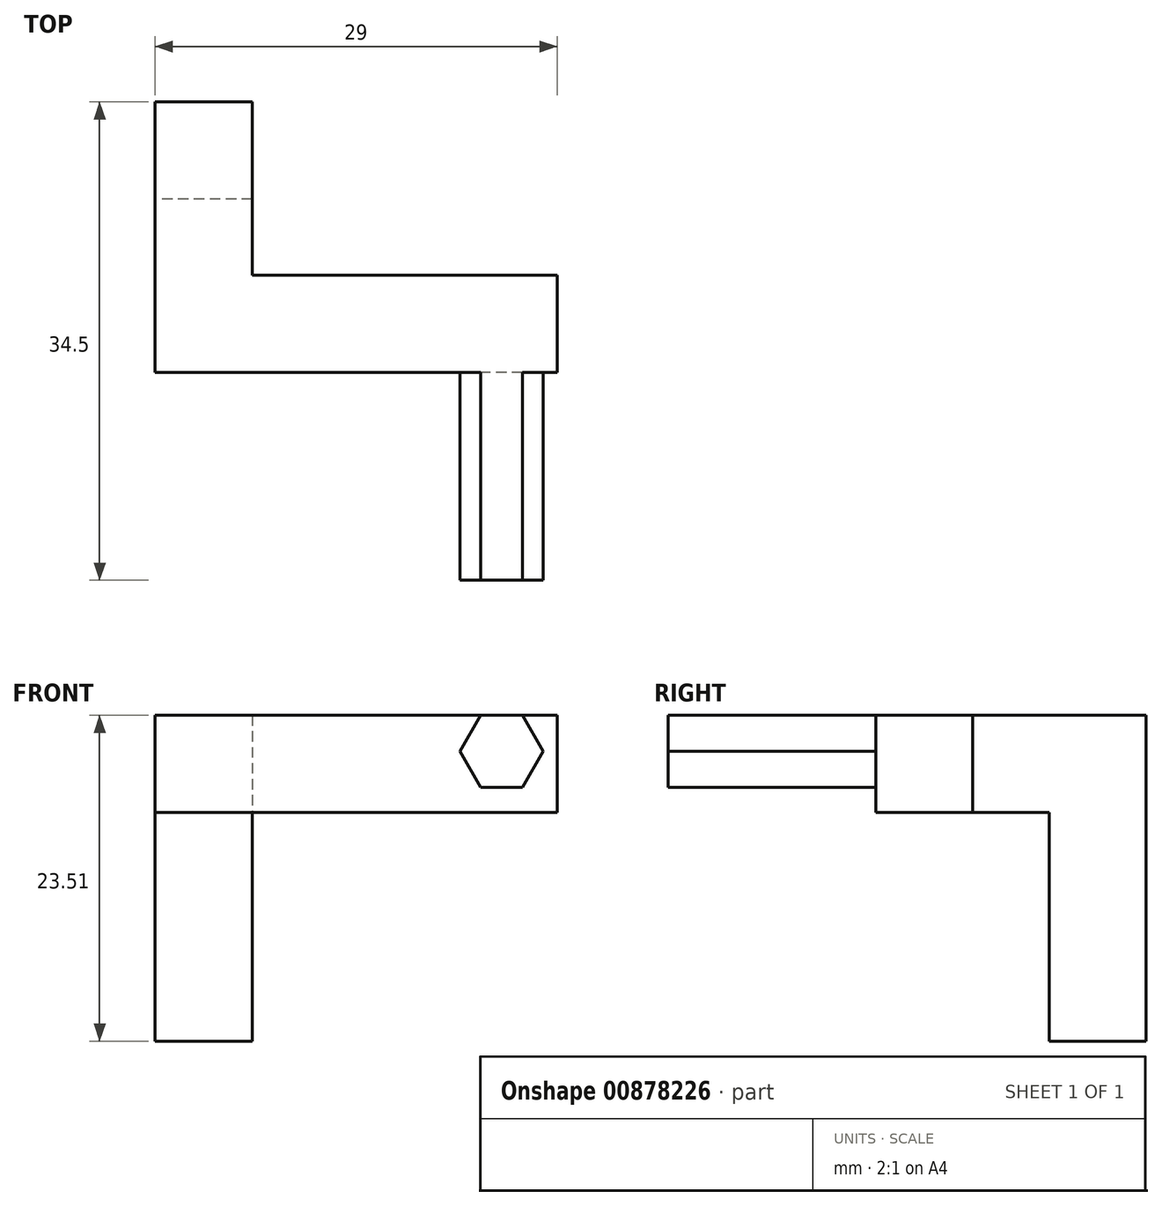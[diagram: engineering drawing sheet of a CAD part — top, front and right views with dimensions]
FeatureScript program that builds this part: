
annotation { "Feature Type Name" : "Feature", "Feature Type Description" : "" }
export const myFeature = defineFeature(function(context is Context, id is Id, definition is map)
    precondition{}
    {
        {
            var Q0;
            Q0=qCreatedBy(makeId("Top.planeOp"),FACE);
            var sketch = newSketch(context, id + "F0", { "sketchPlane" : qUnion([Q0])});
            skLineSegment(sketch, "E0.bottom", {"start": v(3.5, -3.5) * mm, "end": v(-3.5, -3.5) * mm});
            skLineSegment(sketch, "E0.top", {"start": v(3.5, 3.5) * mm, "end": v(-3.5, 3.5) * mm});
            skLineSegment(sketch, "E0.left", {"start": v(3.5, -3.5) * mm, "end": v(3.5, 3.5) * mm});
            skLineSegment(sketch, "E0.right", {"start": v(-3.5, -3.5) * mm, "end": v(-3.5, 3.5) * mm});
            skPoint(sketch, "E0.middle", {"position": v(0, 0) * mm});
            skSolve(sketch);
        }
        {
            var Q0;
            Q0 = qSketchRegion(id + "F0", true);
            extrude(context, id + "F1", {"entities" : qUnion([Q0]), "oppositeDirection" : true, "depth" : 16.5 * mm, "offsetDistance" : 25.4 * mm});
        }
        {
            var Q0;
            Q0=qCreatedBy(makeId("Top.planeOp"),FACE);
            var sketch = newSketch(context, id + "F2", { "sketchPlane" : qUnion([Q0])});
            skLineSegment(sketch, "E1", {"start": v(0, 0) * mm, "end": v(0, -16) * mm});
            skLineSegment(sketch, "E2", {"start": v(0, -16) * mm, "end": v(25.5, -16) * mm});
            skSolve(sketch);
        }
        {
            var Q0;
            Q0=makeQuery(id+"F1.opExtrude","SWEPT_FACE",FACE,{"disambiguationData":[OSD([sQuery(id+"F0.wireOp",EDGE,"E0.top")])]});
            var sketch = newSketch(context, id + "F3", { "sketchPlane" : qUnion([Q0])});
            skLineSegment(sketch, "E3.0.0", {"start": v(3.5, 0) * mm, "end": v(-3.5, 0) * mm, "construction": true});
            skLineSegment(sketch, "E3.0.1", {"start": v(-3.5, 0) * mm, "end": v(-3.5, -16.51) * mm, "construction": true});
            skLineSegment(sketch, "E3.0.2", {"start": v(-3.5, -16.51) * mm, "end": v(3.5, -16.51) * mm, "construction": true});
            skLineSegment(sketch, "E3.0.3", {"start": v(3.5, -16.51) * mm, "end": v(3.5, 0) * mm, "construction": true});
            skLineSegment(sketch, "E4.bottom", {"start": v(-3.5, 0) * mm, "end": v(3.5, 0) * mm});
            skLineSegment(sketch, "E4.top", {"start": v(-3.5, 7) * mm, "end": v(3.5, 7) * mm});
            skLineSegment(sketch, "E4.left", {"start": v(-3.5, 0) * mm, "end": v(-3.5, 7) * mm});
            skLineSegment(sketch, "E4.right", {"start": v(3.5, 0) * mm, "end": v(3.5, 7) * mm});
            skSolve(sketch);
        }
        {
            var Q0;
            Q0 = qSketchRegion(id + "F3", true);
            var Q1;
            Q1=sQuery(id+"F2.wireOp",VERTEX,"E1.end");
            extrude(context, id + "F4", {"entities" : qUnion([Q0]), "operationType" : NewBodyOperationType.ADD, "endBound" : BoundingType.UP_TO_VERTEX, "oppositeDirection" : true, "depth" : 25.4 * mm, "endBoundEntityVertex" : qUnion([Q1]), "offsetDistance" : 25.4 * mm});
        }
        {
            var Q0;
            Q0=makeQuery(id+"F4.boolean.opBoolean","MERGE",FACE,{"derivedFrom":[makeQuery(id+"F1.opExtrude","SWEPT_FACE",FACE,{"disambiguationData":[OSD([sQuery(id+"F0.wireOp",EDGE,"E0.left")])]}),makeQuery(id+"F4.opExtrude","SWEPT_FACE",FACE,{"disambiguationData":[OSD([sQuery(id+"F3.wireOp",EDGE,"E4.left")])]})]});
            var sketch = newSketch(context, id + "F5", { "sketchPlane" : qUnion([Q0])});
            skLineSegment(sketch, "E5.0.0", {"start": v(3.5, -16.51) * mm, "end": v(3.5, 7) * mm, "construction": true});
            skLineSegment(sketch, "E5.0.1", {"start": v(3.5, 7) * mm, "end": v(-16, 7) * mm, "construction": true});
            skLineSegment(sketch, "E5.0.2", {"start": v(-16, 7) * mm, "end": v(-16, 0) * mm});
            skLineSegment(sketch, "E5.0.3", {"start": v(-16, 0) * mm, "end": v(-3.5, 0) * mm, "construction": true});
            skLineSegment(sketch, "E5.0.4", {"start": v(-3.5, 0) * mm, "end": v(-3.5, -16.51) * mm, "construction": true});
            skLineSegment(sketch, "E5.0.5", {"start": v(-3.5, -16.51) * mm, "end": v(3.5, -16.51) * mm, "construction": true});
            skLineSegment(sketch, "E6.bottom", {"start": v(-16, 7) * mm, "end": v(-9, 7) * mm});
            skLineSegment(sketch, "E6.top", {"start": v(-16, 0) * mm, "end": v(-9, 0) * mm});
            skLineSegment(sketch, "E6.right", {"start": v(-9, 7) * mm, "end": v(-9, 0) * mm});
            skLineSegment(sketch, "E7", {"start": v(-9, 0) * mm, "end": v(-16, 0) * mm});
            skSolve(sketch);
        }
        {
            var Q0;
            Q0 = qSketchRegion(id + "F5", true);
            var Q1;
            Q1=sQuery(id+"F2.wireOp",VERTEX,"E2.end");
            extrude(context, id + "F6", {"entities" : qUnion([Q0]), "operationType" : NewBodyOperationType.ADD, "endBound" : BoundingType.UP_TO_VERTEX, "depth" : 25.4 * mm, "endBoundEntityVertex" : qUnion([Q1]), "offsetDistance" : 25.4 * mm});
        }
        {
            var Q0;
            Q0=makeQuery(id+"F6.boolean.opBoolean","MERGE",FACE,{"derivedFrom":[makeQuery(id+"F4.opExtrude","CAP_FACE",FACE,{"disambiguationData":[OSD([sQuery(id+"F3.wireOp",EDGE,"E4.bottom"),sQuery(id+"F3.wireOp",EDGE,"E4.top"),sQuery(id+"F3.wireOp",EDGE,"E4.left"),sQuery(id+"F3.wireOp",EDGE,"E4.right")])],"isStart":false}),makeQuery(id+"F6.opExtrude","SWEPT_FACE",FACE,{"disambiguationData":[OSD([sQuery(id+"F5.wireOp",EDGE,"E5.0.2")])]})]});
            var sketch = newSketch(context, id + "F7", { "sketchPlane" : qUnion([Q0])});
            skLineSegment(sketch, "E8.0.0", {"start": v(-3.5, 0) * mm, "end": v(25.5, 0) * mm, "construction": true});
            skLineSegment(sketch, "E8.0.1", {"start": v(25.5, 0) * mm, "end": v(25.5, 7) * mm, "construction": true});
            skLineSegment(sketch, "E8.0.2", {"start": v(25.5, 7) * mm, "end": v(-3.5, 7) * mm, "construction": true});
            skLineSegment(sketch, "E8.0.3", {"start": v(-3.5, 7) * mm, "end": v(-3.5, 0) * mm, "construction": true});
            skLineSegment(sketch, "E9", {"start": v(25.5, 3.5) * mm, "end": v(17.5, 3.5) * mm, "construction": true});
            skLineSegment(sketch, "E10", {"start": v(21.5, 3.5) * mm, "end": v(21.5, 4.4) * mm});
            skCircle(sketch, "E11.cCircle", {"center": v(21.5, 4.4) * mm, "radius": 3 * mm, "construction": true});
            skLineSegment(sketch, "E11.0", {"start": v(20, 7) * mm, "end": v(23, 7) * mm});
            skLineSegment(sketch, "E11.1", {"start": v(23, 7) * mm, "end": v(24.5, 4.4) * mm});
            skLineSegment(sketch, "E11.2", {"start": v(24.5, 4.4) * mm, "end": v(23, 1.8) * mm});
            skLineSegment(sketch, "E11.3", {"start": v(23, 1.8) * mm, "end": v(20, 1.8) * mm});
            skLineSegment(sketch, "E11.4", {"start": v(20, 1.8) * mm, "end": v(18.5, 4.4) * mm});
            skLineSegment(sketch, "E11.5", {"start": v(18.5, 4.4) * mm, "end": v(20, 7) * mm});
            skSolve(sketch);
        }
        {
            var Q0;
            Q0 = qSketchRegion(id + "F7", true);
            extrude(context, id + "F8", {"entities" : qUnion([Q0]), "operationType" : NewBodyOperationType.ADD, "depth" : 15 * mm, "offsetDistance" : 25.4 * mm});
        }
    });
